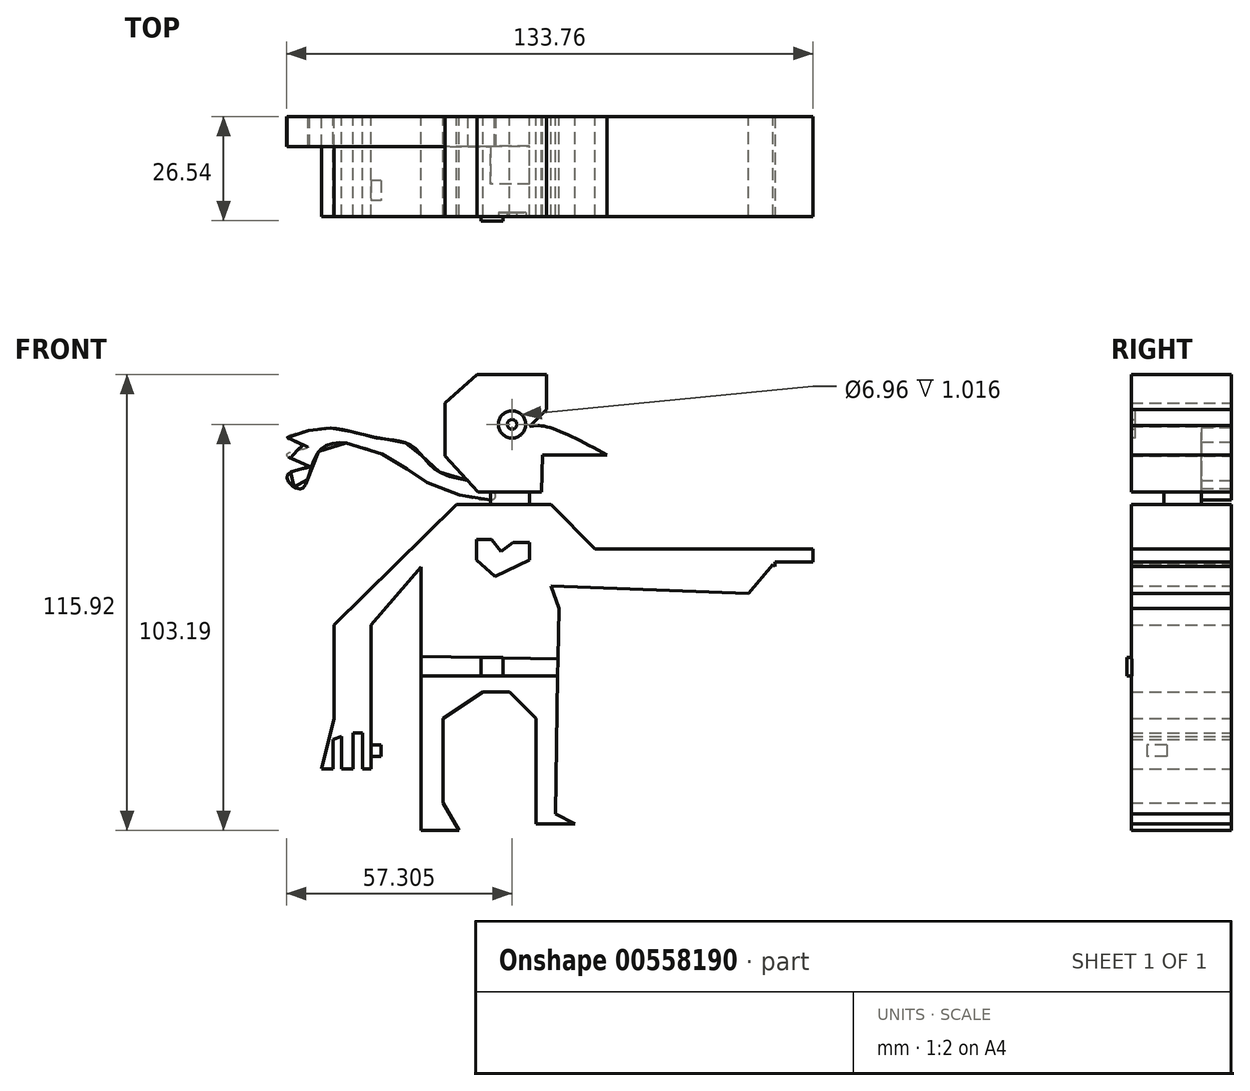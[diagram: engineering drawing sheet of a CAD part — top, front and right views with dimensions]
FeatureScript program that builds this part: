
annotation { "Feature Type Name" : "Feature", "Feature Type Description" : "" }
export const myFeature = defineFeature(function(context is Context, id is Id, definition is map)
    precondition{}
    {
        {
            var Q0;
            Q0=qCreatedBy(makeId("Front.planeOp"),FACE);
            var sketch = newSketch(context, id + "F0", { "sketchPlane" : qUnion([Q0])});
            skLineSegment(sketch, "E0", {"start": v(-27.47, -60.25) * mm, "end": v(-17.83, -60.25) * mm});
            skLineSegment(sketch, "E1", {"start": v(-17.83, -60.25) * mm, "end": v(-21.93, -53.26) * mm});
            skLineSegment(sketch, "E2", {"start": v(-21.93, -53.26) * mm, "end": v(-21.93, -31.81) * mm});
            skLineSegment(sketch, "E3", {"start": v(-21.93, -31.81) * mm, "end": v(-11.8, -25.06) * mm});
            skLineSegment(sketch, "E4", {"start": v(-11.8, -25.06) * mm, "end": v(-5.06, -25.06) * mm});
            skLineSegment(sketch, "E5", {"start": v(-5.06, -25.06) * mm, "end": v(1.69, -31.81) * mm});
            skLineSegment(sketch, "E6", {"start": v(1.69, -31.81) * mm, "end": v(1.69, -53.5) * mm});
            skLineSegment(sketch, "E7", {"start": v(1.69, -53.5) * mm, "end": v(11.57, -58.56) * mm});
            skLineSegment(sketch, "E8", {"start": v(11.57, -58.56) * mm, "end": v(1.69, -58.56) * mm});
            skLineSegment(sketch, "E9", {"start": v(1.69, -58.56) * mm, "end": v(1.69, -53.5) * mm});
            skLineSegment(sketch, "E10", {"start": v(-27.47, -60.25) * mm, "end": v(-27.47, 6.75) * mm});
            skLineSegment(sketch, "E11", {"start": v(-27.47, 6.75) * mm, "end": v(-40.25, -7.95) * mm});
            skLineSegment(sketch, "E12", {"start": v(-40.25, -7.95) * mm, "end": v(-40.25, -31.81) * mm});
            skLineSegment(sketch, "E13", {"start": v(-40.25, -31.81) * mm, "end": v(-49.64, -31.81) * mm});
            skLineSegment(sketch, "E14", {"start": v(-49.64, -31.81) * mm, "end": v(-49.64, -7.95) * mm});
            skLineSegment(sketch, "E15", {"start": v(-49.64, -7.95) * mm, "end": v(-18.56, 22.65) * mm});
            skLineSegment(sketch, "E16", {"start": v(5.54, 22.65) * mm, "end": v(-18.56, 22.65) * mm});
            skLineSegment(sketch, "E17", {"start": v(5.54, 22.65) * mm, "end": v(16.63, 11.33) * mm});
            skLineSegment(sketch, "E18", {"start": v(16.63, 11.33) * mm, "end": v(55.67, 11.33) * mm});
            skLineSegment(sketch, "E19", {"start": v(55.67, 11.33) * mm, "end": v(55.67, 0) * mm});
            skLineSegment(sketch, "E20", {"start": v(55.67, 0) * mm, "end": v(5.54, 1.93) * mm});
            skLineSegment(sketch, "E21", {"start": v(5.54, 1.93) * mm, "end": v(7.47, -3.86) * mm});
            skLineSegment(sketch, "E22", {"start": v(7.47, -3.86) * mm, "end": v(6.63, -56.03) * mm});
            skLineSegment(sketch, "E23", {"start": v(55.67, 11.33) * mm, "end": v(72.06, 11.33) * mm});
            skLineSegment(sketch, "E24", {"start": v(72.06, 11.33) * mm, "end": v(72.06, 7.95) * mm});
            skLineSegment(sketch, "E25", {"start": v(72.06, 7.95) * mm, "end": v(62.42, 7.95) * mm});
            skLineSegment(sketch, "E26", {"start": v(62.42, 7.95) * mm, "end": v(62.42, 0) * mm});
            skLineSegment(sketch, "E27", {"start": v(62.42, 0) * mm, "end": v(55.67, 0) * mm});
            skLineSegment(sketch, "E28", {"start": v(-40.25, -31.81) * mm, "end": v(-40.25, -44.58) * mm});
            skLineSegment(sketch, "E29", {"start": v(-40.25, -44.58) * mm, "end": v(-42.41, -44.58) * mm});
            skLineSegment(sketch, "E30", {"start": v(-42.41, -44.58) * mm, "end": v(-42.41, -35.43) * mm});
            skLineSegment(sketch, "E31", {"start": v(-42.41, -35.43) * mm, "end": v(-44.82, -35.43) * mm});
            skLineSegment(sketch, "E32", {"start": v(-44.82, -35.43) * mm, "end": v(-44.82, -44.58) * mm});
            skLineSegment(sketch, "E33", {"start": v(-44.82, -44.58) * mm, "end": v(-47.72, -44.58) * mm});
            skLineSegment(sketch, "E34", {"start": v(-47.72, -44.58) * mm, "end": v(-47.72, -36.4) * mm});
            skLineSegment(sketch, "E35", {"start": v(-47.72, -36.4) * mm, "end": v(-49.89, -37.11) * mm});
            skLineSegment(sketch, "E36", {"start": v(-49.89, -37.11) * mm, "end": v(-49.89, -44.58) * mm});
            skLineSegment(sketch, "E37", {"start": v(-49.89, -44.58) * mm, "end": v(-52.78, -44.58) * mm});
            skLineSegment(sketch, "E38", {"start": v(-52.78, -44.58) * mm, "end": v(-49.64, -31.81) * mm});
            skLineSegment(sketch, "E39", {"start": v(-6.5, 22.65) * mm, "end": v(-6.5, 28.68) * mm});
            skPoint(sketch, "E39.endSnap0", {"position": v(-6.5, 22.65) * mm});
            skLineSegment(sketch, "E40", {"start": v(-6.5, 28.68) * mm, "end": v(-15.42, 28.68) * mm});
            skLineSegment(sketch, "E41", {"start": v(-15.42, 28.68) * mm, "end": v(-22.65, 34.94) * mm});
            skLineSegment(sketch, "E42", {"start": v(-22.65, 34.94) * mm, "end": v(-22.65, 46.75) * mm});
            skLineSegment(sketch, "E43", {"start": v(-22.65, 46.75) * mm, "end": v(-14.22, 51.57) * mm});
            skLineSegment(sketch, "E44", {"start": v(-14.22, 51.57) * mm, "end": v(2.4, 51.57) * mm});
            skLineSegment(sketch, "E45", {"start": v(2.4, 51.57) * mm, "end": v(9.88, 45.79) * mm});
            skLineSegment(sketch, "E46", {"start": v(9.88, 45.79) * mm, "end": v(9.88, 35.19) * mm});
            skLineSegment(sketch, "E47", {"start": v(9.88, 35.19) * mm, "end": v(2.65, 28.68) * mm});
            skLineSegment(sketch, "E48", {"start": v(2.65, 28.68) * mm, "end": v(-6.5, 28.68) * mm});
            skSolve(sketch);
        }
        {
            var Q0;
            Q0 = qSketchRegion(id + "F0", true);
            extrude(context, id + "F1", {"entities" : qUnion([Q0]), "depth" : 25.4 * mm, "offsetDistance" : 25.4 * mm});
        }
        {
            var Q0;
            Q0=qCreatedBy(makeId("Front.planeOp"),FACE);
            var sketch = newSketch(context, id + "F2", { "sketchPlane" : qUnion([Q0])});
            skLineSegment(sketch, "E49.bottom", {"start": v(-34.95, 58.37) * mm, "end": v(28.4, 58.37) * mm});
            skLineSegment(sketch, "E49.top", {"start": v(-34.95, 24.62) * mm, "end": v(28.4, 24.62) * mm});
            skLineSegment(sketch, "E49.left", {"start": v(-34.95, 58.37) * mm, "end": v(-34.95, 24.62) * mm});
            skLineSegment(sketch, "E49.right", {"start": v(28.4, 58.37) * mm, "end": v(28.4, 24.62) * mm});
            skSolve(sketch);
        }
        {
            var Q0;
            Q0=makeQuery(id+"F2.imprint","IMPRINT",FACE,{"disambiguationData":[TD([[makeQuery(id+"F2.imprint","IMPRINT",EDGE,{"derivedFrom":sQuery(id+"F2.wireOp",EDGE,"E49.bottom")}),-1.0]])]});
            extrude(context, id + "F3", {"entities" : qUnion([Q0]), "operationType" : NewBodyOperationType.REMOVE, "depth" : 60.2 * mm, "offsetDistance" : 25.4 * mm});
        }
        {
            var Q0;
            Q0=makeQuery(id+"F1.opExtrude","SWEPT_FACE",FACE,{"disambiguationData":[OSD([sQuery(id+"F0.wireOp",EDGE,"E16")])]});
            var sketch = newSketch(context, id + "F4", { "sketchPlane" : qUnion([Q0])});
            skLineSegment(sketch, "E50.bottom", {"start": v(-9.93, -7.53) * mm, "end": v(0, -7.53) * mm});
            skLineSegment(sketch, "E50.top", {"start": v(-9.93, -17.15) * mm, "end": v(0, -17.15) * mm});
            skLineSegment(sketch, "E50.left", {"start": v(-9.93, -7.53) * mm, "end": v(-9.93, -17.15) * mm});
            skLineSegment(sketch, "E50.right", {"start": v(0, -7.53) * mm, "end": v(0, -17.15) * mm});
            skSolve(sketch);
        }
        {
            var Q0;
            Q0=makeQuery(id+"F4.imprint","IMPRINT",FACE,{"disambiguationData":[TD([[makeQuery(id+"F4.imprint","IMPRINT",EDGE,{"derivedFrom":sQuery(id+"F4.wireOp",EDGE,"E50.bottom")}),-1.0]])]});
            extrude(context, id + "F5", {"entities" : qUnion([Q0]), "operationType" : NewBodyOperationType.ADD, "depth" : 3.3 * mm, "offsetDistance" : 25.4 * mm});
        }
        {
            var Q0;
            Q0=qCreatedBy(makeId("Front.planeOp"),FACE);
            var sketch = newSketch(context, id + "F6", { "sketchPlane" : qUnion([Q0])});
            skLineSegment(sketch, "E51", {"start": v(3.13, 25.79) * mm, "end": v(-13.01, 25.79) * mm});
            skLineSegment(sketch, "E52", {"start": v(-13.01, 25.79) * mm, "end": v(-21.45, 34.94) * mm});
            skLineSegment(sketch, "E53", {"start": v(-21.45, 34.94) * mm, "end": v(-21.45, 48.44) * mm});
            skLineSegment(sketch, "E54", {"start": v(-21.45, 48.44) * mm, "end": v(-13.25, 55.67) * mm});
            skLineSegment(sketch, "E55", {"start": v(-13.25, 55.67) * mm, "end": v(4.34, 55.67) * mm});
            skLineSegment(sketch, "E56", {"start": v(4.34, 55.67) * mm, "end": v(4.34, 46.75) * mm});
            skLineSegment(sketch, "E57", {"start": v(4.34, 46.75) * mm, "end": v(0, 42.41) * mm});
            skFitSpline(sketch, "E58", {"points": [v(0, 42.41) * mm, v(4.1, 42.41) * mm, v(19.76, 35.19) * mm], "startDerivative": vector(10.74, 1.76) * mm, "endDerivative": vector(26.93, -14.37) * mm});
            skLineSegment(sketch, "E59", {"start": v(19.76, 35.19) * mm, "end": v(3.37, 35.19) * mm});
            skLineSegment(sketch, "E60", {"start": v(3.37, 35.19) * mm, "end": v(3.13, 25.79) * mm});
            skSolve(sketch);
        }
        {
            var Q0;
            Q0 = qSketchRegion(id + "F6", true);
            extrude(context, id + "F7", {"entities" : qUnion([Q0]), "operationType" : NewBodyOperationType.ADD, "depth" : 25.4 * mm, "offsetDistance" : 25.4 * mm});
        }
        {
            var Q0;
            Q0=makeQuery(id+"F7.opExtrude","CAP_FACE",FACE,{"disambiguationData":[OSD([sQuery(id+"F6.wireOp",EDGE,"E51"),sQuery(id+"F6.wireOp",EDGE,"E52"),sQuery(id+"F6.wireOp",EDGE,"E53"),sQuery(id+"F6.wireOp",EDGE,"E54"),sQuery(id+"F6.wireOp",EDGE,"E55"),sQuery(id+"F6.wireOp",EDGE,"E56"),sQuery(id+"F6.wireOp",EDGE,"E57"),sQuery(id+"F6.wireOp",EDGE,"E58"),sQuery(id+"F6.wireOp",EDGE,"E59"),sQuery(id+"F6.wireOp",EDGE,"E60")])],"isStart":false});
            var sketch = newSketch(context, id + "F8", { "sketchPlane" : qUnion([Q0])});
            skCircle(sketch, "E61", {"center": v(-4.4, 42.94) * mm, "radius": 3.48 * mm});
            skSolve(sketch);
        }
        {
            var Q0;
            Q0 = qSketchRegion(id + "F8", true);
            extrude(context, id + "F9", {"entities" : qUnion([Q0]), "operationType" : NewBodyOperationType.REMOVE, "oppositeDirection" : true, "depth" : 1.02 * mm, "offsetDistance" : 25.4 * mm});
        }
        {
            var Q0;
            Q0=makeQuery(id+"F9.boolean.opBoolean","COPY",FACE,{"derivedFrom":makeQuery(id+"F9.opExtrude","CAP_FACE",FACE,{"disambiguationData":[OSD([sQuery(id+"F8.wireOp",EDGE,"E61")])],"isStart":false})});
            var sketch = newSketch(context, id + "F10", { "sketchPlane" : qUnion([Q0])});
            skCircle(sketch, "E62", {"center": v(-4.4, 42.94) * mm, "radius": 1.21 * mm});
            skSolve(sketch);
        }
        {
            var Q0;
            Q0 = qSketchRegion(id + "F10", true);
            extrude(context, id + "F11", {"entities" : qUnion([Q0]), "operationType" : NewBodyOperationType.ADD, "depth" : 1.02 * mm, "offsetDistance" : 25.4 * mm});
        }
        {
            var Q0;
            Q0=makeQuery(id+"F1.opExtrude","SWEPT_EDGE",EDGE,{"disambiguationData":[OSD([sQuery(id+"F0.wireOp",EDGE,"E19"),sQuery(id+"F0.wireOp",EDGE,"E20"),sQuery(id+"F0.wireOp",EDGE,"E27")])]});
            cPoint(context, id + "F12", {"entities" : qUnion([Q0]), "parameter" : 0.5});
        }
        {
            var Q0;
            Q0=makeQuery(id+"F1.opExtrude","CAP_VERTEX",VERTEX,{"disambiguationData":[OSD([sQuery(id+"F0.wireOp",EDGE,"E25"),sQuery(id+"F0.wireOp",EDGE,"E26")])],"isStart":true});
            var Q1;
            Q1=makeQuery(id+"F1.opExtrude","CAP_VERTEX",VERTEX,{"disambiguationData":[OSD([sQuery(id+"F0.wireOp",EDGE,"E25"),sQuery(id+"F0.wireOp",EDGE,"E26")])],"isStart":false});
            var Q2;
            Q2 = qCreatedBy(id + "F12" ,VERTEX);
            cPlane(context, id + "F13", {"entities" : qUnion([Q0, Q1, Q2]), "cplaneType" : CPlaneType.THREE_POINT, "offset" : 25.4 * mm, "width" : 152.4 * mm, "height" : 152.4 * mm});
        }
        {
            var Q0;
            Q0=qCreatedBy(id+"F13.planeOp",FACE);
            var sketch = newSketch(context, id + "F14", { "sketchPlane" : qUnion([Q0])});
            skLineSegment(sketch, "E63.bottom", {"start": v(30.12, 45.63) * mm, "end": v(-19.2, 45.63) * mm});
            skLineSegment(sketch, "E63.top", {"start": v(30.12, 26.46) * mm, "end": v(-19.2, 26.46) * mm});
            skLineSegment(sketch, "E63.left", {"start": v(30.12, 45.63) * mm, "end": v(30.12, 26.46) * mm});
            skLineSegment(sketch, "E63.right", {"start": v(-19.2, 45.63) * mm, "end": v(-19.2, 26.46) * mm});
            skSolve(sketch);
        }
        {
            var Q0;
            Q0 = qSketchRegion(id + "F14", true);
            extrude(context, id + "F15", {"entities" : qUnion([Q0]), "operationType" : NewBodyOperationType.REMOVE, "oppositeDirection" : true, "depth" : 53.85 * mm, "offsetDistance" : 25.4 * mm});
        }
        {
            var Q0;
            Q0=makeQuery(id+"F1.opExtrude","SWEPT_FACE",FACE,{"disambiguationData":[OSD([sQuery(id+"F0.wireOp",EDGE,"E12"),sQuery(id+"F0.wireOp",EDGE,"E28")])]});
            var sketch = newSketch(context, id + "F16", { "sketchPlane" : qUnion([Q0])});
            skLineSegment(sketch, "E64.bottom", {"start": v(-16.35, -38.55) * mm, "end": v(-21.4, -38.55) * mm});
            skLineSegment(sketch, "E64.top", {"start": v(-16.35, -41.38) * mm, "end": v(-21.4, -41.38) * mm});
            skLineSegment(sketch, "E64.left", {"start": v(-16.35, -38.55) * mm, "end": v(-16.35, -41.38) * mm});
            skLineSegment(sketch, "E64.right", {"start": v(-21.4, -38.55) * mm, "end": v(-21.4, -41.38) * mm});
            skSolve(sketch);
        }
        {
            var Q0;
            Q0 = qSketchRegion(id + "F16", true);
            extrude(context, id + "F17", {"entities" : qUnion([Q0]), "operationType" : NewBodyOperationType.ADD, "depth" : 2.54 * mm, "offsetDistance" : 25.4 * mm});
        }
        {
            var Q0;
            Q0=qCreatedBy(makeId("Front.planeOp"),FACE);
            var sketch = newSketch(context, id + "F18", { "sketchPlane" : qUnion([Q0])});
            skFitSpline(sketch, "E65", {"points": [v(-9.88, 26.75) * mm, v(-22.9, 30.85) * mm, v(-29.64, 37.35) * mm, v(-35.43, 39.04) * mm, v(-38.8, 39.52) * mm, v(-47.72, 41.7) * mm, v(-54.46, 41.7) * mm, v(-61.45, 39.28) * mm, v(-56.4, 37.11) * mm, v(-61.7, 35.19) * mm, v(-55.91, 32.3) * mm, v(-61.45, 30.12) * mm, v(-58.08, 26.5) * mm, v(-52.78, 36.87) * mm, v(-34.22, 33.74) * mm, v(-25.06, 27.71) * mm, v(-8.92, 24.1) * mm, v(-9.88, 26.75) * mm]});
            skSolve(sketch);
        }
        {
            var Q0;
            Q0 = qSketchRegion(id + "F18", true);
            extrude(context, id + "F19", {"entities" : qUnion([Q0]), "operationType" : NewBodyOperationType.ADD, "depth" : 7.62 * mm, "offsetDistance" : 25.4 * mm});
        }
        {
            var Q0;
            Q0=makeQuery(id+"F1.opExtrude","CAP_FACE",FACE,{"disambiguationData":[OSD([sQuery(id+"F0.wireOp",EDGE,"E0"),sQuery(id+"F0.wireOp",EDGE,"E1"),sQuery(id+"F0.wireOp",EDGE,"E2"),sQuery(id+"F0.wireOp",EDGE,"E3"),sQuery(id+"F0.wireOp",EDGE,"E4"),sQuery(id+"F0.wireOp",EDGE,"E5"),sQuery(id+"F0.wireOp",EDGE,"E6"),sQuery(id+"F0.wireOp",EDGE,"E7"),sQuery(id+"F0.wireOp",EDGE,"E8"),sQuery(id+"F0.wireOp",EDGE,"E9"),sQuery(id+"F0.wireOp",EDGE,"E10"),sQuery(id+"F0.wireOp",EDGE,"E11"),sQuery(id+"F0.wireOp",EDGE,"E12"),sQuery(id+"F0.wireOp",EDGE,"E14"),sQuery(id+"F0.wireOp",EDGE,"E15"),sQuery(id+"F0.wireOp",EDGE,"E16"),sQuery(id+"F0.wireOp",EDGE,"E17"),sQuery(id+"F0.wireOp",EDGE,"E18"),sQuery(id+"F0.wireOp",EDGE,"E20"),sQuery(id+"F0.wireOp",EDGE,"E21"),sQuery(id+"F0.wireOp",EDGE,"E22"),sQuery(id+"F0.wireOp",EDGE,"E23"),sQuery(id+"F0.wireOp",EDGE,"E24"),sQuery(id+"F0.wireOp",EDGE,"E25"),sQuery(id+"F0.wireOp",EDGE,"E26"),sQuery(id+"F0.wireOp",EDGE,"E27"),sQuery(id+"F0.wireOp",EDGE,"E28"),sQuery(id+"F0.wireOp",EDGE,"E29"),sQuery(id+"F0.wireOp",EDGE,"E30"),sQuery(id+"F0.wireOp",EDGE,"E31"),sQuery(id+"F0.wireOp",EDGE,"E32"),sQuery(id+"F0.wireOp",EDGE,"E33"),sQuery(id+"F0.wireOp",EDGE,"E34"),sQuery(id+"F0.wireOp",EDGE,"E35"),sQuery(id+"F0.wireOp",EDGE,"E36"),sQuery(id+"F0.wireOp",EDGE,"E37"),sQuery(id+"F0.wireOp",EDGE,"E38")])],"isStart":false});
            var sketch = newSketch(context, id + "F20", { "sketchPlane" : qUnion([Q0])});
            skLineSegment(sketch, "E66", {"start": v(-27.47, -20.97) * mm, "end": v(7.2, -20.97) * mm});
            skLineSegment(sketch, "E67", {"start": v(7.2, -20.97) * mm, "end": v(7.26, -16.63) * mm});
            skLineSegment(sketch, "E68", {"start": v(7.26, -16.63) * mm, "end": v(-27.47, -16.06) * mm});
            skLineSegment(sketch, "E69", {"start": v(-27.47, -16.06) * mm, "end": v(-27.47, -20.97) * mm});
            skSolve(sketch);
        }
        {
            var Q0;
            Q0 = qSketchRegion(id + "F20", true);
            extrude(context, id + "F21", {"entities" : qUnion([Q0]), "operationType" : NewBodyOperationType.REMOVE, "oppositeDirection" : true, "depth" : 0.13 * mm, "offsetDistance" : 25.4 * mm});
        }
        {
            var Q0;
            {var subQ0=sQuery(id+"F0.wireOp",EDGE,"E36");var subQ1=sQuery(id+"F0.wireOp",EDGE,"E35");var subQ2=sQuery(id+"F0.wireOp",EDGE,"E34");var subQ3=sQuery(id+"F0.wireOp",EDGE,"E33");var subQ4=sQuery(id+"F0.wireOp",EDGE,"E32");var subQ5=sQuery(id+"F0.wireOp",EDGE,"E31");var subQ6=sQuery(id+"F0.wireOp",EDGE,"E30");var subQ7=sQuery(id+"F0.wireOp",EDGE,"E29");var subQ8=sQuery(id+"F0.wireOp",EDGE,"E26");var subQ9=sQuery(id+"F0.wireOp",EDGE,"E25");var subQ10=sQuery(id+"F0.wireOp",EDGE,"E24");var subQ11=sQuery(id+"F0.wireOp",EDGE,"E22");var subQ12=sQuery(id+"F0.wireOp",EDGE,"E14");var subQ13=sQuery(id+"F0.wireOp",EDGE,"E28");var subQ14=sQuery(id+"F0.wireOp",EDGE,"E12");var subQ15=sQuery(id+"F0.wireOp",EDGE,"E11");var subQ16=sQuery(id+"F0.wireOp",EDGE,"E10");var subQ17=sQuery(id+"F0.wireOp",EDGE,"E15");var subQ18=sQuery(id+"F0.wireOp",EDGE,"E16");var subQ19=sQuery(id+"F0.wireOp",EDGE,"E17");var subQ20=sQuery(id+"F0.wireOp",EDGE,"E23");var subQ21=sQuery(id+"F0.wireOp",EDGE,"E18");var subQ22=sQuery(id+"F0.wireOp",EDGE,"E20");var subQ23=sQuery(id+"F0.wireOp",EDGE,"E21");var subQ24=sQuery(id+"F0.wireOp",EDGE,"E37");var subQ25=sQuery(id+"F0.wireOp",EDGE,"E38");Q0=makeQuery(id+"F21.boolean.opBoolean","SPLIT",FACE,{"disambiguationData":[TD([makeQuery(id+"F1.opExtrude","SWEPT_FACE",FACE,{"disambiguationData":[OSD([subQ15])]})])],"derivedFrom":makeQuery(id+"F1.opExtrude","CAP_FACE",FACE,{"disambiguationData":[OSD([sQuery(id+"F0.wireOp",EDGE,"E0"),sQuery(id+"F0.wireOp",EDGE,"E1"),sQuery(id+"F0.wireOp",EDGE,"E2"),sQuery(id+"F0.wireOp",EDGE,"E3"),sQuery(id+"F0.wireOp",EDGE,"E4"),sQuery(id+"F0.wireOp",EDGE,"E5"),sQuery(id+"F0.wireOp",EDGE,"E6"),sQuery(id+"F0.wireOp",EDGE,"E7"),sQuery(id+"F0.wireOp",EDGE,"E8"),sQuery(id+"F0.wireOp",EDGE,"E9"),subQ16,subQ15,subQ14,subQ12,subQ17,subQ18,subQ19,subQ21,subQ22,subQ23,subQ11,subQ20,subQ10,subQ9,subQ8,sQuery(id+"F0.wireOp",EDGE,"E27"),subQ13,subQ7,subQ6,subQ5,subQ4,subQ3,subQ2,subQ1,subQ0,subQ24,subQ25])],"isStart":false})});}
            var sketch = newSketch(context, id + "F22", { "sketchPlane" : qUnion([Q0])});
            skLineSegment(sketch, "E70", {"start": v(-8.68, 4.34) * mm, "end": v(-13.4, 8.44) * mm});
            skLineSegment(sketch, "E71", {"start": v(-13.4, 8.44) * mm, "end": v(-13.4, 10.6) * mm});
            skLineSegment(sketch, "E72", {"start": v(-13.4, 10.6) * mm, "end": v(-13.4, 13.74) * mm});
            skLineSegment(sketch, "E73", {"start": v(-13.4, 13.74) * mm, "end": v(-9.64, 13.74) * mm});
            skLineSegment(sketch, "E74", {"start": v(-9.64, 13.74) * mm, "end": v(-7.23, 10.6) * mm});
            skLineSegment(sketch, "E75", {"start": v(-7.23, 10.6) * mm, "end": v(-4.17, 12.96) * mm});
            skLineSegment(sketch, "E76", {"start": v(-4.17, 12.96) * mm, "end": v(0, 12.96) * mm});
            skLineSegment(sketch, "E77", {"start": v(0, 12.96) * mm, "end": v(0, 8.44) * mm});
            skLineSegment(sketch, "E78", {"start": v(0, 8.44) * mm, "end": v(-8.68, 4.34) * mm});
            skSolve(sketch);
        }
        {
            var Q0;
            Q0 = qSketchRegion(id + "F22", true);
            extrude(context, id + "F23", {"entities" : qUnion([Q0]), "operationType" : NewBodyOperationType.ADD, "depth" : 0.01 * mm, "offsetDistance" : 25.4 * mm});
        }
        {
            var Q0;
            Q0=makeQuery(id+"F21.boolean.opBoolean","COPY",FACE,{"derivedFrom":makeQuery(id+"F21.opExtrude","CAP_FACE",FACE,{"disambiguationData":[OSD([sQuery(id+"F20.wireOp",EDGE,"E66"),sQuery(id+"F20.wireOp",EDGE,"E67"),sQuery(id+"F20.wireOp",EDGE,"E68"),sQuery(id+"F20.wireOp",EDGE,"E69")])],"isStart":false})});
            var sketch = newSketch(context, id + "F24", { "sketchPlane" : qUnion([Q0])});
            skLineSegment(sketch, "E79.bottom", {"start": v(-12.3, -16.3) * mm, "end": v(-6.75, -16.3) * mm});
            skLineSegment(sketch, "E79.top", {"start": v(-12.3, -20.97) * mm, "end": v(-6.75, -20.97) * mm});
            skLineSegment(sketch, "E79.left", {"start": v(-12.3, -16.3) * mm, "end": v(-12.3, -20.97) * mm});
            skLineSegment(sketch, "E79.right", {"start": v(-6.75, -16.3) * mm, "end": v(-6.75, -20.97) * mm});
            skSolve(sketch);
        }
        {
            var Q0;
            Q0 = qSketchRegion(id + "F24", true);
            extrude(context, id + "F25", {"entities" : qUnion([Q0]), "operationType" : NewBodyOperationType.ADD, "depth" : 1.27 * mm, "offsetDistance" : 25.4 * mm});
        }
    });
